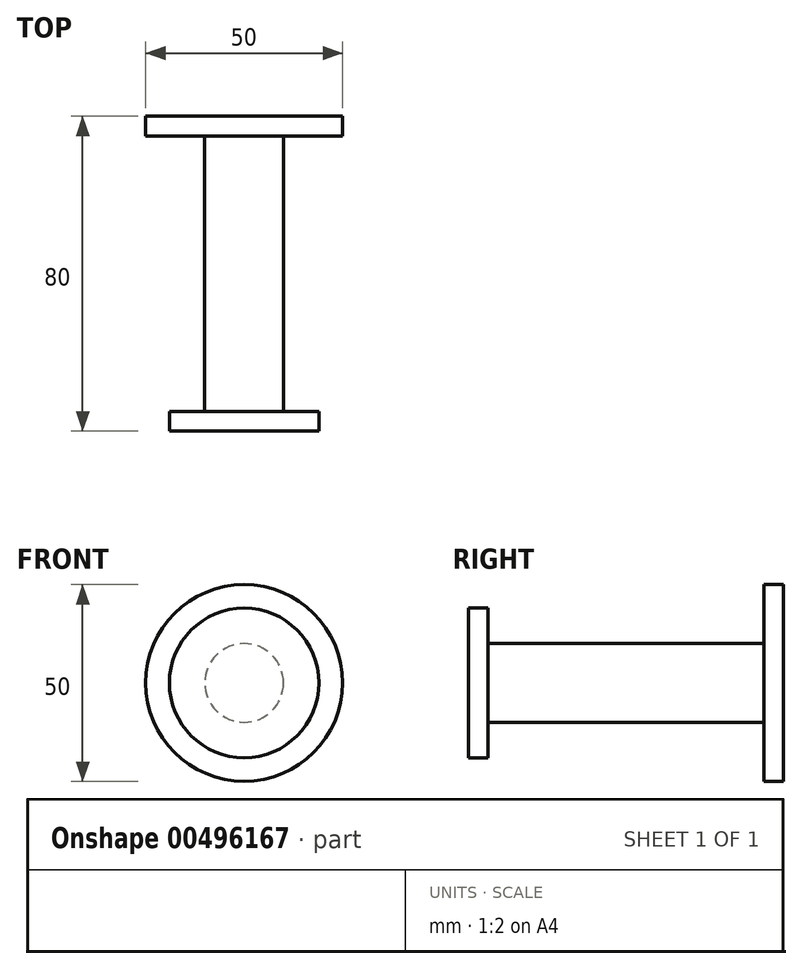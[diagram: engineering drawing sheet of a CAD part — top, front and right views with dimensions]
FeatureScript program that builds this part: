
annotation { "Feature Type Name" : "Feature", "Feature Type Description" : "" }
export const myFeature = defineFeature(function(context is Context, id is Id, definition is map)
    precondition{}
    {
        {
            var Q0;
            Q0=qCreatedBy(makeId("Front.planeOp"),FACE);
            var sketch = newSketch(context, id + "F0", { "sketchPlane" : qUnion([Q0])});
            skCircle(sketch, "E0", {"center": v(0, 0) * mm, "radius": 25 * mm});
            skSolve(sketch);
        }
        {
            var Q0;
            Q0=qSketchRegion(id+"F0",true);
            var Q1;
            Q1=makeQuery(id+"F0.imprint","IMPRINT",FACE,{"disambiguationData":[TD([[makeQuery(id+"F0.imprint","IMPRINT",EDGE,{"derivedFrom":sQuery(id+"F0.wireOp",EDGE,"E0")}),1.0]])]});
            extrude(context, id + "F1", {"entities" : qUnion([Q0, Q1]), "depth" : 5 * mm});
        }
        {
            var Q0;
            Q0=makeQuery(id+"F1.opExtrude","CAP_FACE",FACE,{"disambiguationData":[OSD([sQuery(id+"F0.wireOp",EDGE,"E0")])],"isStart":false});
            var sketch = newSketch(context, id + "F2", { "sketchPlane" : qUnion([Q0])});
            skCircle(sketch, "E1", {"center": v(0, 0) * mm, "radius": 10 * mm});
            skSolve(sketch);
        }
        {
            var Q0;
            Q0=makeQuery(id+"F2.imprint","IMPRINT",FACE,{"disambiguationData":[TD([[makeQuery(id+"F2.imprint","IMPRINT",EDGE,{"derivedFrom":sQuery(id+"F2.wireOp",EDGE,"E1")}),1.0]])]});
            extrude(context, id + "F3", {"entities" : qUnion([Q0]), "operationType" : NewBodyOperationType.ADD, "depth" : 70 * mm});
        }
        {
            var Q0;
            Q0=makeQuery(id+"F3.opExtrude","CAP_FACE",FACE,{"disambiguationData":[OSD([sQuery(id+"F2.wireOp",EDGE,"E1")])],"isStart":false});
            var sketch = newSketch(context, id + "F4", { "sketchPlane" : qUnion([Q0])});
            skCircle(sketch, "E2", {"center": v(0, 0) * mm, "radius": 19 * mm});
            skSolve(sketch);
        }
        {
            var Q0;
            Q0=qSketchRegion(id+"F4",true);
            extrude(context, id + "F5", {"entities" : qUnion([Q0]), "operationType" : NewBodyOperationType.ADD, "depth" : 5 * mm});
        }
    });
